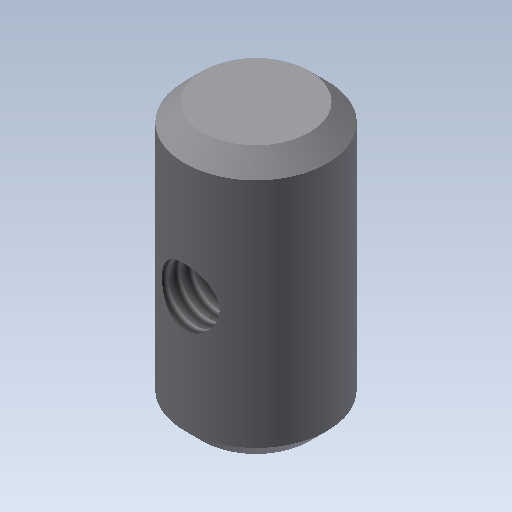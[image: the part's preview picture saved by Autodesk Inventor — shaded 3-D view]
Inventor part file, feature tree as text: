
AUTODESK INVENTOR PART (.ipt)
format: ipt  version: 2020.2 (Build 242310000, 310)  size: 102,400 bytes
history: native  units: mm
features: sketch x2, extrude x1, plane x1, hole x1, chamfer x1
ambient origin geometry x8: Origin, YZ Plane, XZ Plane, XY Plane, X Axis, Y Axis, Z Axis, Center Point
bodies: Volumenkörper1 (feature_tree)
feature tree (6):
  extrude  "Extrusion1"  Depth=15.0mm TaperAngle=0.0deg
  plane  "Arbeitsebene1"
  hole  "Bohrung1"  [1 undecoded]
  chamfer  "Fase1"  [1 undecoded]
  sketch  "Skizze1"  dims[d0=8.0mm d1=15.0mm d2=0.0mm]
  sketch  "Skizze2"  dims[d3=7.5mm d4=3.242mm d5=10.0mm d6=4.0mm d7=2.0mm d8=90.0deg d9=8.0mm d10=20.594885mm d11=1.0mm d12=2.0mm d13=45.0deg]
note: 2 required parameter values undecoded (feature->parameter linkage not recoverable at this tier; creation-order binding heuristic only, values carry confidence <= 0.55)
